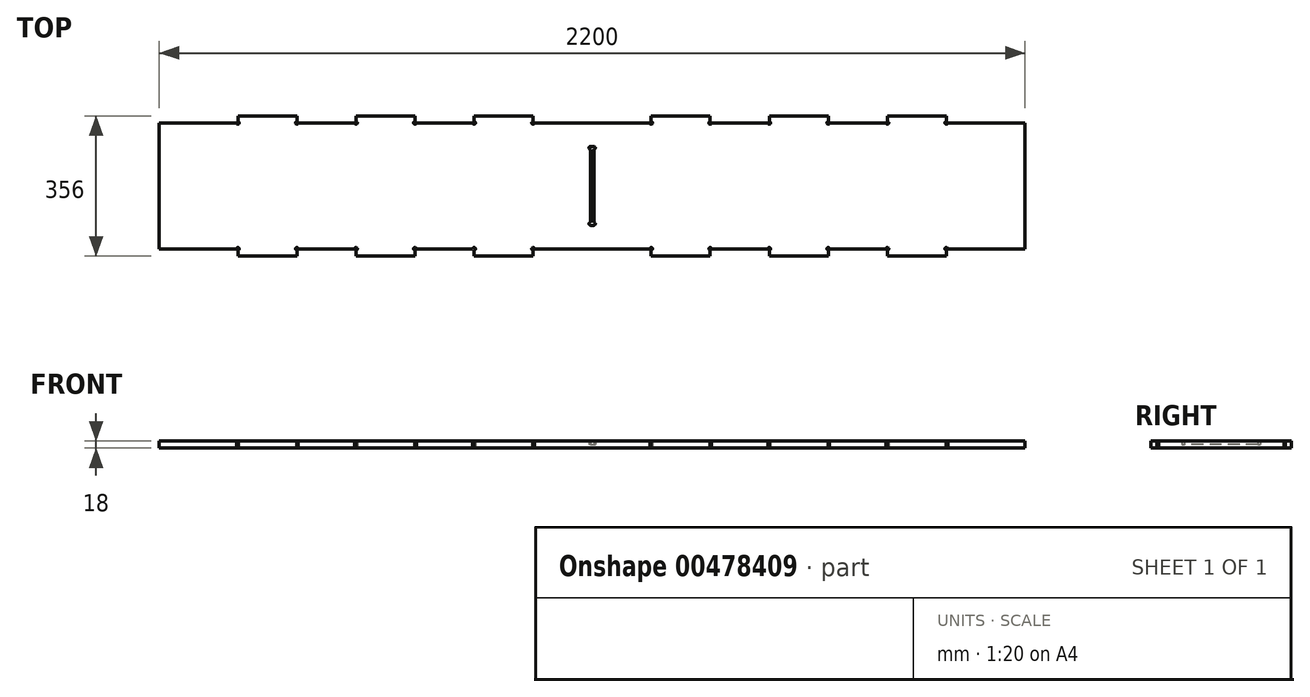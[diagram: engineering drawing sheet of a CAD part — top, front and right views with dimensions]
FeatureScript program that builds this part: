
annotation { "Feature Type Name" : "Feature", "Feature Type Description" : "" }
export const myFeature = defineFeature(function(context is Context, id is Id, definition is map)
    precondition{}
    {
        {
            var Q0;
            Q0=qCreatedBy(makeId("Top.planeOp"),FACE);
            var sketch = newSketch(context, id + "F0", { "sketchPlane" : qUnion([Q0])});
            skLineSegment(sketch, "E0.right", {"start": v(-27.4, 97.87) * mm, "end": v(-27.4, -62.13) * mm, "construction": true});
            skLineSegment(sketch, "E1.top", {"start": v(-1127.4, -62.13) * mm, "end": v(-930.9, -62.13) * mm});
            skLineSegment(sketch, "E2", {"start": v(-927.4, -65.63) * mm, "end": v(-927.4, -80.13) * mm});
            skLineSegment(sketch, "E3", {"start": v(-927.4, -80.13) * mm, "end": v(-777.4, -80.13) * mm});
            skLineSegment(sketch, "E4", {"start": v(-777.4, -80.13) * mm, "end": v(-777.4, -62.13) * mm});
            skLineSegment(sketch, "E5", {"start": v(-777.4, -62.13) * mm, "end": v(-627.4, -62.13) * mm});
            skLineSegment(sketch, "E6.0", {"start": v(-1127.4, 97.87) * mm, "end": v(-27.4, 97.87) * mm, "construction": true});
            skArc(sketch, "E7", {"start": v(-927.4, -65.63) * mm, "mid": v(-924.92, -59.66) * mm, "end": v(-930.9, -62.13) * mm});
            skLineSegment(sketch, "E8", {"start": v(-1127.4, 97.87) * mm, "end": v(-1127.4, -62.13) * mm});
            skPoint(sketch, "E9.orphan", {"position": v(-1073.9, -62.13) * mm});
            skArc(sketch, "E10", {"start": v(-777.4, -65.63) * mm, "mid": v(-779.87, -59.66) * mm, "end": v(-773.9, -62.13) * mm});
            skPoint(sketch, "E11.orphan", {"position": v(-777.4, -76.63) * mm});
            skPoint(sketch, "E12.orphan", {"position": v(-923.9, -80.13) * mm});
            skPoint(sketch, "E13.orphan", {"position": v(-780.9, -80.13) * mm});
            skLineSegment(sketch, "E14.1.0.0", {"start": v(-627.4, -80.13) * mm, "end": v(-477.4, -80.13) * mm});
            skLineSegment(sketch, "E14.1.0.1", {"start": v(-477.4, -80.13) * mm, "end": v(-477.4, -65.63) * mm});
            skArc(sketch, "E14.1.0.2", {"start": v(-627.4, -65.63) * mm, "mid": v(-624.92, -59.66) * mm, "end": v(-630.9, -62.13) * mm});
            skPoint(sketch, "E14.1.0.3", {"position": v(-623.9, -80.13) * mm});
            skArc(sketch, "E14.1.0.4", {"start": v(-477.4, -65.63) * mm, "mid": v(-479.87, -59.66) * mm, "end": v(-473.9, -62.13) * mm});
            skLineSegment(sketch, "E14.1.0.5", {"start": v(-627.4, -65.63) * mm, "end": v(-627.4, -80.13) * mm});
            skPoint(sketch, "E14.1.0.6", {"position": v(-477.4, -76.63) * mm});
            skPoint(sketch, "E14.1.0.7", {"position": v(-480.9, -80.13) * mm});
            skLineSegment(sketch, "E14.1.0.8", {"start": v(-473.9, -62.13) * mm, "end": v(-330.9, -62.13) * mm});
            skLineSegment(sketch, "E14.2.0.0", {"start": v(-327.4, -80.13) * mm, "end": v(-177.4, -80.13) * mm});
            skLineSegment(sketch, "E14.2.0.1", {"start": v(-177.4, -80.13) * mm, "end": v(-177.4, -65.63) * mm});
            skArc(sketch, "E14.2.0.2", {"start": v(-327.4, -65.63) * mm, "mid": v(-324.92, -59.66) * mm, "end": v(-330.9, -62.13) * mm});
            skPoint(sketch, "E14.2.0.3", {"position": v(-323.9, -80.13) * mm});
            skArc(sketch, "E14.2.0.4", {"start": v(-177.4, -65.63) * mm, "mid": v(-179.87, -59.66) * mm, "end": v(-173.9, -62.13) * mm});
            skLineSegment(sketch, "E14.2.0.5", {"start": v(-327.4, -65.63) * mm, "end": v(-327.4, -80.13) * mm});
            skPoint(sketch, "E14.2.0.6", {"position": v(-177.4, -76.63) * mm});
            skPoint(sketch, "E14.2.0.7", {"position": v(-180.9, -80.13) * mm});
            skLineSegment(sketch, "E14.2.0.8", {"start": v(-173.9, -62.13) * mm, "end": v(-27.4, -62.13) * mm});
            skLineSegment(sketch, "E14.direction1", {"start": v(-927.4, -80.13) * mm, "end": v(-627.4, -80.13) * mm, "construction": true});
            skLineSegment(sketch, "E15.MirrorCS", {"start": v(-27.4, -92.13) * mm, "end": v(-27.4, 97.87) * mm, "construction": true});
            skPoint(sketch, "E16.orphan", {"position": v(-1127.4, 257.87) * mm});
            skPoint(sketch, "E17.orphan", {"position": v(-27.4, 257.87) * mm});
            skPoint(sketch, "E18.orphan", {"position": v(-27.4, 287.87) * mm});
            skPoint(sketch, "E19.orphan", {"position": v(-1127.4, -62.13) * mm});
            skArc(sketch, "E20.MirrorCS", {"start": v(722.6, -65.63) * mm, "mid": v(725.08, -59.66) * mm, "end": v(719.1, -62.13) * mm});
            skArc(sketch, "E21.MirrorCS", {"start": v(572.6, -65.63) * mm, "mid": v(570.13, -59.66) * mm, "end": v(576.1, -62.13) * mm});
            skLineSegment(sketch, "E22.MirrorCS", {"start": v(572.6, -65.63) * mm, "end": v(572.6, -80.13) * mm});
            skLineSegment(sketch, "E23.MirrorCS", {"start": v(722.6, -80.13) * mm, "end": v(722.6, -62.13) * mm});
            skArc(sketch, "E24.MirrorCS", {"start": v(872.6, -65.63) * mm, "mid": v(870.13, -59.66) * mm, "end": v(876.1, -62.13) * mm});
            skLineSegment(sketch, "E25.MirrorCS", {"start": v(272.6, -65.63) * mm, "end": v(272.6, -80.13) * mm});
            skArc(sketch, "E26.MirrorCS", {"start": v(272.6, -65.63) * mm, "mid": v(270.13, -59.66) * mm, "end": v(276.1, -62.13) * mm});
            skLineSegment(sketch, "E27.MirrorCS", {"start": v(872.6, -65.63) * mm, "end": v(872.6, -80.13) * mm});
            skLineSegment(sketch, "E28.MirrorCS", {"start": v(122.6, -80.13) * mm, "end": v(122.6, -65.63) * mm});
            skArc(sketch, "E29.MirrorCS", {"start": v(122.6, -65.63) * mm, "mid": v(125.08, -59.66) * mm, "end": v(119.1, -62.13) * mm});
            skLineSegment(sketch, "E30.MirrorCS", {"start": v(422.6, -80.13) * mm, "end": v(422.6, -65.63) * mm});
            skArc(sketch, "E31.MirrorCS", {"start": v(422.6, -65.63) * mm, "mid": v(425.08, -59.66) * mm, "end": v(419.1, -62.13) * mm});
            skPoint(sketch, "E32.MirrorP", {"position": v(722.6, -76.63) * mm});
            skPoint(sketch, "E33.MirrorP", {"position": v(726.1, -80.13) * mm});
            skLineSegment(sketch, "E34.MirrorCS", {"start": v(872.6, -80.13) * mm, "end": v(722.6, -80.13) * mm});
            skLineSegment(sketch, "E35.MirrorCS", {"start": v(1072.6, 97.87) * mm, "end": v(1072.6, -62.13) * mm});
            skLineSegment(sketch, "E36.MirrorCS", {"start": v(572.6, -80.13) * mm, "end": v(422.6, -80.13) * mm});
            skLineSegment(sketch, "E37.MirrorCS", {"start": v(872.6, -80.13) * mm, "end": v(572.6, -80.13) * mm, "construction": true});
            skPoint(sketch, "E38.MirrorP", {"position": v(422.6, -76.63) * mm});
            skPoint(sketch, "E39.MirrorP", {"position": v(1019.1, -62.13) * mm});
            skPoint(sketch, "E40.MirrorP", {"position": v(122.6, -76.63) * mm});
            skLineSegment(sketch, "E41.MirrorCS", {"start": v(272.6, -80.13) * mm, "end": v(122.6, -80.13) * mm});
            skLineSegment(sketch, "E42.MirrorCS", {"start": v(119.1, -62.13) * mm, "end": v(-27.4, -62.13) * mm});
            skLineSegment(sketch, "E43.MirrorCS", {"start": v(419.1, -62.13) * mm, "end": v(276.1, -62.13) * mm});
            skLineSegment(sketch, "E44.MirrorCS", {"start": v(722.6, -62.13) * mm, "end": v(572.6, -62.13) * mm});
            skPoint(sketch, "E45.MirrorP", {"position": v(869.1, -80.13) * mm});
            skPoint(sketch, "E46.MirrorP", {"position": v(569.1, -80.13) * mm});
            skPoint(sketch, "E47.MirrorP", {"position": v(426.1, -80.13) * mm});
            skPoint(sketch, "E48.MirrorP", {"position": v(126.1, -80.13) * mm});
            skPoint(sketch, "E49.MirrorP", {"position": v(269.1, -80.13) * mm});
            skLineSegment(sketch, "E50.MirrorCS", {"start": v(1072.6, -62.13) * mm, "end": v(876.1, -62.13) * mm});
            skPoint(sketch, "E51.MirrorP", {"position": v(1072.6, -62.13) * mm});
            skArc(sketch, "E52.MirrorCS", {"start": v(-777.4, 261.37) * mm, "mid": v(-779.87, 255.4) * mm, "end": v(-773.9, 257.87) * mm});
            skArc(sketch, "E53.MirrorCS", {"start": v(-327.4, 261.37) * mm, "mid": v(-324.92, 255.4) * mm, "end": v(-330.9, 257.87) * mm});
            skLineSegment(sketch, "E54.MirrorCS", {"start": v(-777.4, 275.87) * mm, "end": v(-777.4, 257.87) * mm});
            skArc(sketch, "E55.MirrorCS", {"start": v(722.6, 261.37) * mm, "mid": v(725.08, 255.4) * mm, "end": v(719.1, 257.87) * mm});
            skLineSegment(sketch, "E56.MirrorCS", {"start": v(572.6, 261.37) * mm, "end": v(572.6, 275.87) * mm});
            skLineSegment(sketch, "E57.MirrorCS", {"start": v(-327.4, 261.37) * mm, "end": v(-327.4, 275.87) * mm});
            skLineSegment(sketch, "E58.MirrorCS", {"start": v(722.6, 275.87) * mm, "end": v(722.6, 257.87) * mm});
            skLineSegment(sketch, "E59.MirrorCS", {"start": v(-627.4, 261.37) * mm, "end": v(-627.4, 275.87) * mm});
            skLineSegment(sketch, "E60.MirrorCS", {"start": v(-927.4, 261.37) * mm, "end": v(-927.4, 275.87) * mm});
            skLineSegment(sketch, "E61.MirrorCS", {"start": v(872.6, 261.37) * mm, "end": v(872.6, 275.87) * mm});
            skArc(sketch, "E62.MirrorCS", {"start": v(-927.4, 261.37) * mm, "mid": v(-924.92, 255.4) * mm, "end": v(-930.9, 257.87) * mm});
            skLineSegment(sketch, "E63.MirrorCS", {"start": v(422.6, 275.87) * mm, "end": v(422.6, 261.37) * mm});
            skArc(sketch, "E64.MirrorCS", {"start": v(272.6, 261.37) * mm, "mid": v(270.13, 255.4) * mm, "end": v(276.1, 257.87) * mm});
            skLineSegment(sketch, "E65.MirrorCS", {"start": v(272.6, 261.37) * mm, "end": v(272.6, 275.87) * mm});
            skLineSegment(sketch, "E66.MirrorCS", {"start": v(-177.4, 275.87) * mm, "end": v(-177.4, 261.37) * mm});
            skLineSegment(sketch, "E67.MirrorCS", {"start": v(122.6, 275.87) * mm, "end": v(122.6, 261.37) * mm});
            skArc(sketch, "E68.MirrorCS", {"start": v(-477.4, 261.37) * mm, "mid": v(-479.87, 255.4) * mm, "end": v(-473.9, 257.87) * mm});
            skLineSegment(sketch, "E69.MirrorCS", {"start": v(-477.4, 275.87) * mm, "end": v(-477.4, 261.37) * mm});
            skArc(sketch, "E70.MirrorCS", {"start": v(572.6, 261.37) * mm, "mid": v(570.13, 255.4) * mm, "end": v(576.1, 257.87) * mm});
            skArc(sketch, "E71.MirrorCS", {"start": v(-627.4, 261.37) * mm, "mid": v(-624.92, 255.4) * mm, "end": v(-630.9, 257.87) * mm});
            skArc(sketch, "E72.MirrorCS", {"start": v(422.6, 261.37) * mm, "mid": v(425.08, 255.4) * mm, "end": v(419.1, 257.87) * mm});
            skArc(sketch, "E73.MirrorCS", {"start": v(-177.4, 261.37) * mm, "mid": v(-179.87, 255.4) * mm, "end": v(-173.9, 257.87) * mm});
            skArc(sketch, "E74.MirrorCS", {"start": v(122.6, 261.37) * mm, "mid": v(125.08, 255.4) * mm, "end": v(119.1, 257.87) * mm});
            skArc(sketch, "E75.MirrorCS", {"start": v(872.6, 261.37) * mm, "mid": v(870.13, 255.4) * mm, "end": v(876.1, 257.87) * mm});
            skLineSegment(sketch, "E76.MirrorCS", {"start": v(-27.4, 97.87) * mm, "end": v(-27.4, 257.87) * mm, "construction": true});
            skPoint(sketch, "E77.MirrorP", {"position": v(-777.4, 272.37) * mm});
            skPoint(sketch, "E78.MirrorP", {"position": v(-780.9, 275.87) * mm});
            skLineSegment(sketch, "E79.MirrorCS", {"start": v(-927.4, 275.87) * mm, "end": v(-777.4, 275.87) * mm});
            skLineSegment(sketch, "E80.MirrorCS", {"start": v(872.6, 275.87) * mm, "end": v(722.6, 275.87) * mm});
            skLineSegment(sketch, "E81.MirrorCS", {"start": v(419.1, 257.87) * mm, "end": v(276.1, 257.87) * mm});
            skLineSegment(sketch, "E82.MirrorCS", {"start": v(-627.4, 275.87) * mm, "end": v(-477.4, 275.87) * mm});
            skPoint(sketch, "E83.MirrorP", {"position": v(-180.9, 275.87) * mm});
            skPoint(sketch, "E84.MirrorP", {"position": v(-477.4, 272.37) * mm});
            skLineSegment(sketch, "E85.MirrorCS", {"start": v(-1127.4, 97.87) * mm, "end": v(-1127.4, 257.87) * mm});
            skPoint(sketch, "E86.MirrorP", {"position": v(-480.9, 275.87) * mm});
            skPoint(sketch, "E87.MirrorP", {"position": v(122.6, 272.37) * mm});
            skPoint(sketch, "E88.MirrorP", {"position": v(-323.9, 275.87) * mm});
            skLineSegment(sketch, "E89.MirrorCS", {"start": v(-777.4, 257.87) * mm, "end": v(-627.4, 257.87) * mm});
            skLineSegment(sketch, "E90.MirrorCS", {"start": v(-173.9, 257.87) * mm, "end": v(-27.4, 257.87) * mm});
            skLineSegment(sketch, "E91.MirrorCS", {"start": v(272.6, 275.87) * mm, "end": v(122.6, 275.87) * mm});
            skLineSegment(sketch, "E92.MirrorCS", {"start": v(-1127.4, 257.87) * mm, "end": v(-930.9, 257.87) * mm});
            skPoint(sketch, "E93.MirrorP", {"position": v(426.1, 275.87) * mm});
            skLineSegment(sketch, "E94.MirrorCS", {"start": v(-473.9, 257.87) * mm, "end": v(-330.9, 257.87) * mm});
            skPoint(sketch, "E95.MirrorP", {"position": v(-923.9, 275.87) * mm});
            skPoint(sketch, "E96.MirrorP", {"position": v(1072.6, 257.87) * mm});
            skLineSegment(sketch, "E97.MirrorCS", {"start": v(572.6, 275.87) * mm, "end": v(422.6, 275.87) * mm});
            skLineSegment(sketch, "E98.MirrorCS", {"start": v(1072.6, 97.87) * mm, "end": v(1072.6, 257.87) * mm});
            skPoint(sketch, "E99.MirrorP", {"position": v(-1073.9, 257.87) * mm});
            skPoint(sketch, "E100.MirrorP", {"position": v(569.1, 275.87) * mm});
            skLineSegment(sketch, "E101.MirrorCS", {"start": v(-27.4, 287.87) * mm, "end": v(-27.4, 97.87) * mm, "construction": true});
            skLineSegment(sketch, "E102.MirrorCS", {"start": v(872.6, 275.87) * mm, "end": v(572.6, 275.87) * mm, "construction": true});
            skPoint(sketch, "E103.MirrorP", {"position": v(-177.4, 272.37) * mm});
            skLineSegment(sketch, "E104.MirrorCS", {"start": v(722.6, 257.87) * mm, "end": v(572.6, 257.87) * mm});
            skLineSegment(sketch, "E105.MirrorCS", {"start": v(-327.4, 275.87) * mm, "end": v(-177.4, 275.87) * mm});
            skLineSegment(sketch, "E106.MirrorCS", {"start": v(-927.4, 275.87) * mm, "end": v(-627.4, 275.87) * mm, "construction": true});
            skPoint(sketch, "E107.MirrorP", {"position": v(269.1, 275.87) * mm});
            skPoint(sketch, "E108.MirrorP", {"position": v(726.1, 275.87) * mm});
            skPoint(sketch, "E109.MirrorP", {"position": v(869.1, 275.87) * mm});
            skPoint(sketch, "E110.MirrorP", {"position": v(126.1, 275.87) * mm});
            skPoint(sketch, "E111.MirrorP", {"position": v(722.6, 272.37) * mm});
            skLineSegment(sketch, "E112.MirrorCS", {"start": v(119.1, 257.87) * mm, "end": v(-27.4, 257.87) * mm});
            skLineSegment(sketch, "E113.MirrorCS", {"start": v(1072.6, 257.87) * mm, "end": v(876.1, 257.87) * mm});
            skPoint(sketch, "E114.MirrorP", {"position": v(1019.1, 257.87) * mm});
            skPoint(sketch, "E115.MirrorP", {"position": v(-623.9, 275.87) * mm});
            skPoint(sketch, "E116.MirrorP", {"position": v(422.6, 272.37) * mm});
            skLineSegment(sketch, "E117", {"start": v(-27.4, 97.87) * mm, "end": v(-22.9, 97.87) * mm, "construction": true});
            skLineSegment(sketch, "E118", {"start": v(-22.9, 97.87) * mm, "end": v(-22.9, 190.87) * mm});
            skLineSegment(sketch, "E119", {"start": v(-22.9, 197.87) * mm, "end": v(-27.4, 197.87) * mm});
            skPoint(sketch, "E119.endSnap0", {"position": v(-27.4, 192.87) * mm});
            skArc(sketch, "E120", {"start": v(-22.9, 190.87) * mm, "mid": v(-19.4, 194.37) * mm, "end": v(-22.9, 197.87) * mm});
            skLineSegment(sketch, "E121.MirrorCS", {"start": v(-31.9, 97.87) * mm, "end": v(-31.9, 190.87) * mm});
            skArc(sketch, "E122.MirrorCS", {"start": v(-31.9, 190.87) * mm, "mid": v(-35.4, 194.37) * mm, "end": v(-31.9, 197.87) * mm});
            skLineSegment(sketch, "E123.MirrorCS", {"start": v(-31.9, 197.87) * mm, "end": v(-27.4, 197.87) * mm});
            skLineSegment(sketch, "E124.MirrorCS", {"start": v(-31.9, 97.87) * mm, "end": v(-31.9, 4.87) * mm});
            skArc(sketch, "E125.MirrorCS", {"start": v(-31.9, 4.87) * mm, "mid": v(-35.4, 1.37) * mm, "end": v(-31.9, -2.13) * mm});
            skLineSegment(sketch, "E126.MirrorCS", {"start": v(-31.9, -2.13) * mm, "end": v(-27.4, -2.13) * mm});
            skArc(sketch, "E127.MirrorCS", {"start": v(-22.9, 4.87) * mm, "mid": v(-19.4, 1.37) * mm, "end": v(-22.9, -2.13) * mm});
            skLineSegment(sketch, "E128.MirrorCS", {"start": v(-22.9, 97.87) * mm, "end": v(-22.9, 4.87) * mm});
            skLineSegment(sketch, "E129.MirrorCS", {"start": v(-22.9, -2.13) * mm, "end": v(-27.4, -2.13) * mm});
            skSolve(sketch);
        }
        {
            var Q0;
            Q0=makeQuery(id+"F0.imprint","IMPRINT",FACE,{"disambiguationData":[TD([[makeQuery(id+"F0.imprint","IMPRINT",EDGE,{"derivedFrom":sQuery(id+"F0.wireOp",EDGE,"E1.top")}),1.0]])]});
            extrude(context, id + "F1", {"entities" : qUnion([Q0]), "depth" : 18 * mm});
        }
        {
            var Q0;
            Q0=makeQuery(id+"F0.imprint","IMPRINT",FACE,{"disambiguationData":[TD([[makeQuery(id+"F0.imprint","IMPRINT",EDGE,{"derivedFrom":sQuery(id+"F0.wireOp",EDGE,"E118")}),1.0]])]});
            extrude(context, id + "F2", {"entities" : qUnion([Q0]), "operationType" : NewBodyOperationType.ADD, "depth" : 9 * mm});
        }
    });
